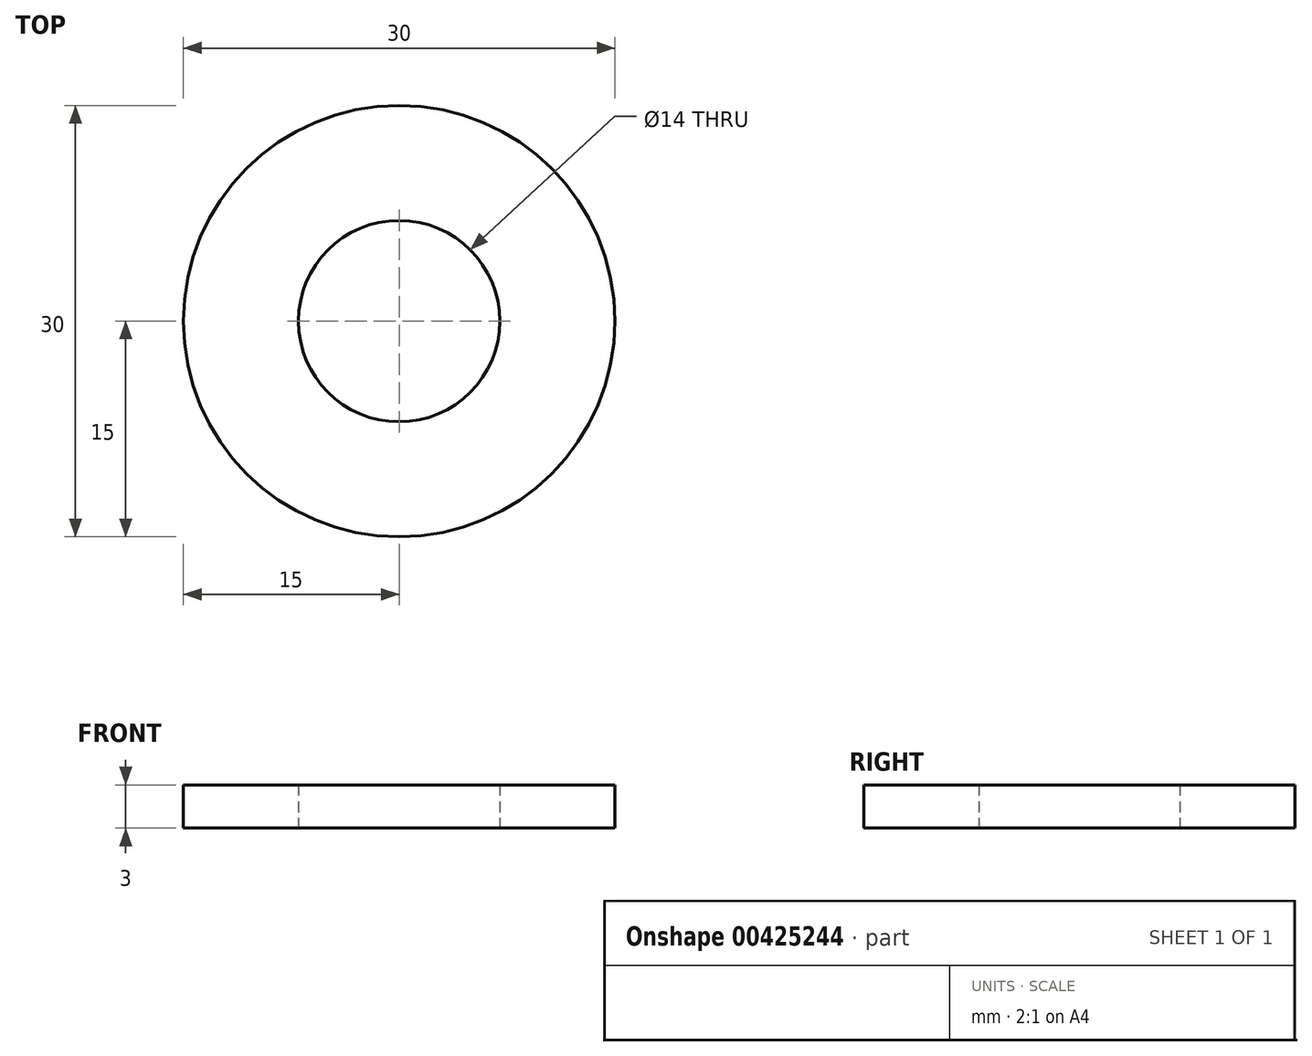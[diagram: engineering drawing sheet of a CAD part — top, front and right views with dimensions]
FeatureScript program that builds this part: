
annotation { "Feature Type Name" : "Feature", "Feature Type Description" : "" }
export const myFeature = defineFeature(function(context is Context, id is Id, definition is map)
    precondition{}
    {
        {
            var Q0;
            Q0=qCreatedBy(makeId("Top.planeOp"),FACE);
            var sketch = newSketch(context, id + "F0", { "sketchPlane" : qUnion([Q0])});
            skCircle(sketch, "E0", {"center": v(0, 0) * mm, "radius": 7 * mm});
            skCircle(sketch, "E1", {"center": v(0, 0) * mm, "radius": 15 * mm});
            skSolve(sketch);
        }
        {
            var Q0;
            Q0=makeQuery(id+"F0.imprint","IMPRINT",FACE,{"disambiguationData":[TD([[makeQuery(id+"F0.imprint","IMPRINT",EDGE,{"derivedFrom":sQuery(id+"F0.wireOp",EDGE,"E0")}),-1.0]])]});
            extrude(context, id + "F1", {"entities" : qUnion([Q0]), "depth" : 3 * mm});
        }
    });
